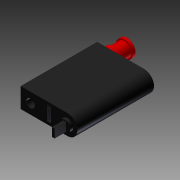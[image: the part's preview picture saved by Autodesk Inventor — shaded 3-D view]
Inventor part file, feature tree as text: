
AUTODESK INVENTOR PART (.ipt)
format: ipt  version: 2011 (Build 150239000, 239)  size: 140,288 bytes
history: native  units: in
note: dims shown in document units (in); Inventor stores cm internally (conversion verified against a paired STEP export)
features: extrude x6, sketch x6
ambient origin geometry x8: Origin, YZ Plane, XZ Plane, XY Plane, X Axis, Y Axis, Z Axis, Center Point
bodies: Solid1 (feature_tree)
feature tree (12):
  extrude  "Extrusion1"  Depth=0.35in
  extrude  "Extrusion2"  TaperAngle=0.0deg  [1 undecoded]
  extrude  "Extrusion3"  Depth=0.15in
  extrude  "Extrusion4"  Depth=0.175in
  extrude  "Extrusion5"  Depth=0.2875in
  extrude  "Extrusion6"  Depth=0.25in
  sketch  "Sketch1"  dims[d0=1.0in d1=0.35in]
  sketch  "Sketch2"  dims[d2=0.0in d3=0.0in]
  sketch  "Sketch3"  dims[d4=0.15in d5=0.15in]
  sketch  "Sketch4"  dims[d6=0.0in d7=0.175in]
  sketch  "Sketch5"  dims[d8=0.175in d9=0.2875in]
  sketch  "Sketch6"  dims[d12=0.075in d13=0.25in d17=1.35in d18=0.0in d19=0.3in d20=0.1in d21=0.0in d22=0.25in d23=0.2in d24=0.0in d25=0.05in d26=0.0in d27=0.2in d28=0.05in d29=0.0in d30=0.15in d31=0.05in d32=0.025in d33=0.075in d34=0.2in d35=0.0in]
note: 1 required parameter value undecoded (feature->parameter linkage not recoverable at this tier; creation-order binding heuristic only, values carry confidence <= 0.55)
